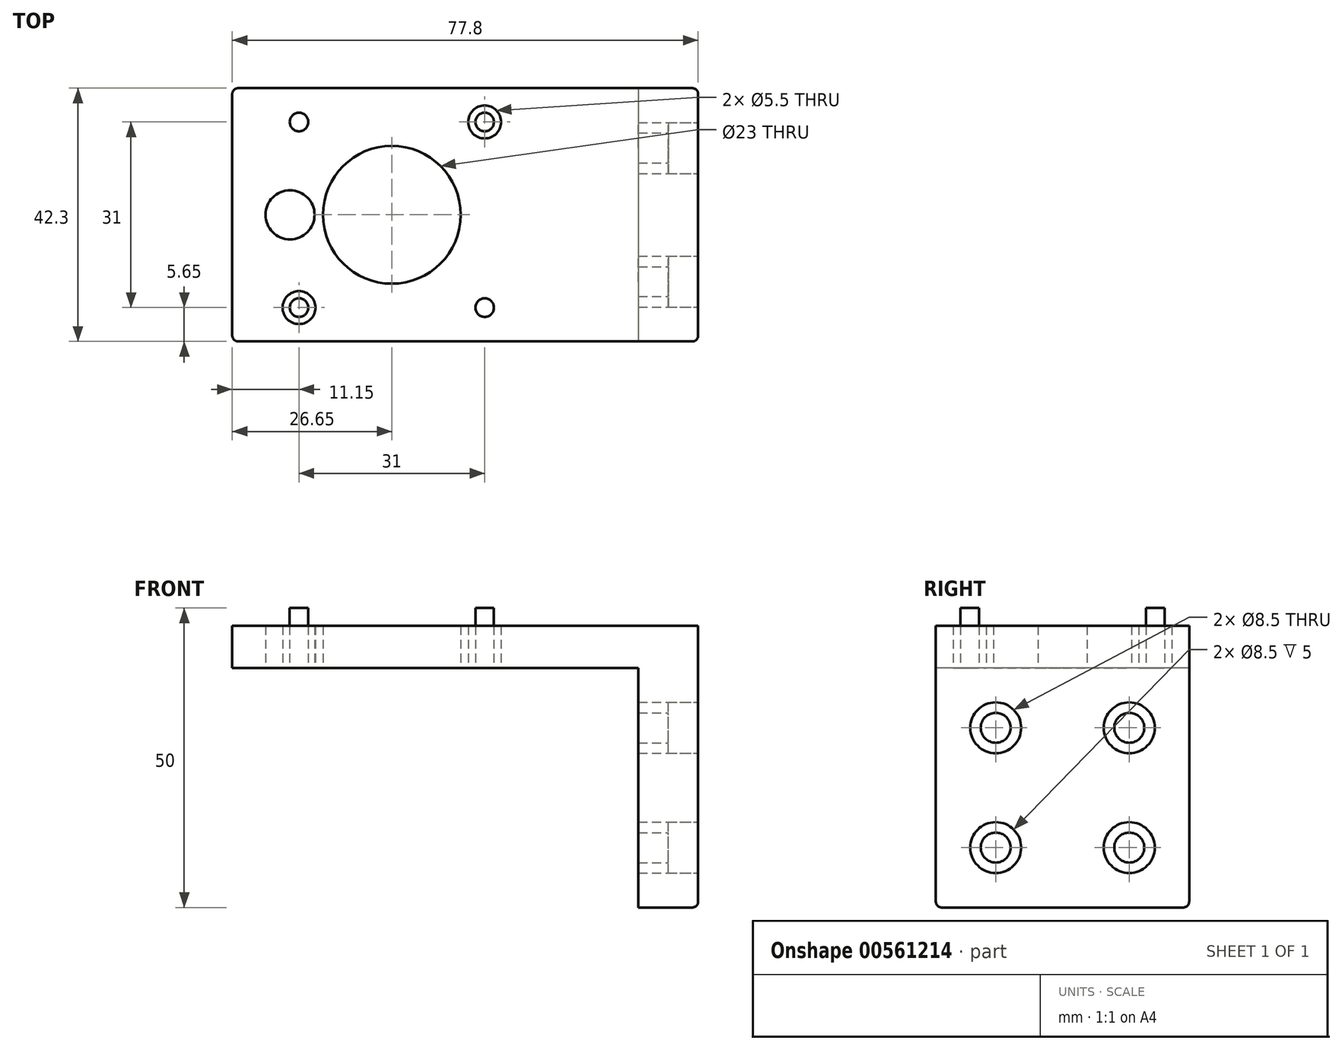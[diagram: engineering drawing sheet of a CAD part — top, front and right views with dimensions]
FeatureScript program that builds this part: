
annotation { "Feature Type Name" : "Feature", "Feature Type Description" : "" }
export const myFeature = defineFeature(function(context is Context, id is Id, definition is map)
    precondition{}
    {
        {
            var Q0;
            Q0=qCreatedBy(makeId("Top.planeOp"),FACE);
            var sketch = newSketch(context, id + "F0", { "sketchPlane" : qUnion([Q0])});
            skCircle(sketch, "E0", {"center": v(0, 0) * mm, "radius": 11.5 * mm});
            skLineSegment(sketch, "E1.bottom", {"start": v(21.15, 21.15) * mm, "end": v(-21.15, 21.15) * mm});
            skLineSegment(sketch, "E1.top", {"start": v(21.15, -21.15) * mm, "end": v(-21.15, -21.15) * mm});
            skLineSegment(sketch, "E1.left", {"start": v(21.15, 21.15) * mm, "end": v(21.15, -21.15) * mm});
            skLineSegment(sketch, "E1.right", {"start": v(-21.15, 21.15) * mm, "end": v(-21.15, -21.15) * mm});
            skCircle(sketch, "E2", {"center": v(-15.5, 15.5) * mm, "radius": 1.55 * mm});
            skLineSegment(sketch, "E3", {"start": v(0, 21.15) * mm, "end": v(0, -21.15) * mm, "construction": true});
            skLineSegment(sketch, "E4", {"start": v(-21.15, 0) * mm, "end": v(21.15, 0) * mm, "construction": true});
            skCircle(sketch, "E5.MirrorC", {"center": v(-15.5, -15.5) * mm, "radius": 1.55 * mm});
            skCircle(sketch, "E6.MirrorC", {"center": v(15.5, 15.5) * mm, "radius": 1.55 * mm});
            skCircle(sketch, "E7.MirrorC", {"center": v(15.5, -15.5) * mm, "radius": 1.55 * mm});
            skLineSegment(sketch, "E8", {"start": v(21.15, 21.15) * mm, "end": v(41.15, 21.15) * mm});
            skLineSegment(sketch, "E9", {"start": v(41.15, 21.15) * mm, "end": v(41.15, -21.15) * mm});
            skLineSegment(sketch, "E10", {"start": v(41.15, -21.15) * mm, "end": v(21.15, -21.15) * mm});
            skLineSegment(sketch, "E11", {"start": v(41.15, 21.15) * mm, "end": v(51.15, 21.15) * mm});
            skLineSegment(sketch, "E12", {"start": v(51.15, 21.15) * mm, "end": v(51.15, -21.15) * mm});
            skLineSegment(sketch, "E13", {"start": v(41.15, -21.15) * mm, "end": v(51.15, -21.15) * mm});
            skCircle(sketch, "E14", {"center": v(-17, 0) * mm, "radius": 4.1 * mm});
            skLineSegment(sketch, "E15", {"start": v(-21.15, 21.15) * mm, "end": v(-26.65, 21.15) * mm});
            skLineSegment(sketch, "E16", {"start": v(-26.65, 21.15) * mm, "end": v(-26.65, -21.15) * mm});
            skLineSegment(sketch, "E17", {"start": v(-26.65, -21.15) * mm, "end": v(-21.15, -21.15) * mm});
            skCircle(sketch, "E18", {"center": v(-15.5, 15.5) * mm, "radius": 2.75 * mm});
            skCircle(sketch, "E19.MirrorC", {"center": v(-15.5, -15.5) * mm, "radius": 2.75 * mm});
            skCircle(sketch, "E20.MirrorC", {"center": v(15.5, 15.5) * mm, "radius": 2.75 * mm});
            skCircle(sketch, "E21.MirrorC", {"center": v(15.5, -15.5) * mm, "radius": 2.75 * mm});
            skSolve(sketch);
        }
        {
            var Q0;
            Q0 = qSketchRegion(id + "F0", true);
            var Q1;
            Q1=makeQuery(id+"F0.imprint","IMPRINT",FACE,{"disambiguationData":[TD([[makeQuery(id+"F0.imprint","IMPRINT",EDGE,{"derivedFrom":sQuery(id+"F0.wireOp",EDGE,"E2")}),-1.0]])]});
            var Q2;
            Q2=makeQuery(id+"F0.imprint","IMPRINT",FACE,{"disambiguationData":[TD([[makeQuery(id+"F0.imprint","IMPRINT",EDGE,{"derivedFrom":sQuery(id+"F0.wireOp",EDGE,"E7.MirrorC")}),-1.0]])]});
            var Q3;
            Q3=makeQuery(id+"F0.imprint","IMPRINT",FACE,{"disambiguationData":[TD([[makeQuery(id+"F0.imprint","IMPRINT",EDGE,{"derivedFrom":sQuery(id+"F0.wireOp",EDGE,"E5.MirrorC")}),1.0]])]});
            var Q4;
            Q4=makeQuery(id+"F0.imprint","IMPRINT",FACE,{"disambiguationData":[TD([[makeQuery(id+"F0.imprint","IMPRINT",EDGE,{"derivedFrom":sQuery(id+"F0.wireOp",EDGE,"E6.MirrorC")}),1.0]])]});
            extrude(context, id + "F1", {"entities" : qUnion([Q0, Q1, Q2, Q3, Q4]), "depth" : 10 * mm, "offsetDistance" : 25 * mm});
        }
        {
            var Q0;
            Q0=makeQuery(id+"F0.imprint","IMPRINT",FACE,{"disambiguationData":[TD([[makeQuery(id+"F0.imprint","IMPRINT",EDGE,{"derivedFrom":sQuery(id+"F0.wireOp",EDGE,"E9")}),1.0]])]});
            extrude(context, id + "F2", {"entities" : qUnion([Q0]), "operationType" : NewBodyOperationType.ADD, "oppositeDirection" : true, "depth" : 40 * mm, "offsetDistance" : 25 * mm});
        }
        {
            var Q0;
            {var subQ0=sQuery(id+"F0.wireOp",EDGE,"E12");Q0=makeQuery(id+"F2.boolean.opBoolean","MERGE",FACE,{"derivedFrom":[makeQuery(id+"F1.opExtrude","SWEPT_FACE",FACE,{"disambiguationData":[OSD([subQ0])]}),makeQuery(id+"F2.opExtrude","SWEPT_FACE",FACE,{"disambiguationData":[OSD([subQ0])]})]});}
            var sketch = newSketch(context, id + "F3", { "sketchPlane" : qUnion([Q0])});
            skCircle(sketch, "E22", {"center": v(-11.15, -30) * mm, "radius": 4.25 * mm});
            skCircle(sketch, "E23", {"center": v(-11.15, -30) * mm, "radius": 2.5 * mm});
            skLineSegment(sketch, "E24", {"start": v(0, 10) * mm, "end": v(0, -40) * mm, "construction": true});
            skCircle(sketch, "E25.MirrorC", {"center": v(11.15, -30) * mm, "radius": 2.5 * mm});
            skCircle(sketch, "E26.MirrorC", {"center": v(11.15, -30) * mm, "radius": 4.25 * mm});
            skLineSegment(sketch, "E27", {"start": v(11.15, -30) * mm, "end": v(11.15, -20) * mm, "construction": true});
            skLineSegment(sketch, "E28", {"start": v(-11.15, -30) * mm, "end": v(-11.15, -20) * mm, "construction": true});
            skLineSegment(sketch, "E29", {"start": v(-11.15, -20) * mm, "end": v(11.15, -20) * mm, "construction": true});
            skCircle(sketch, "E30.MirrorC", {"center": v(-11.15, -10) * mm, "radius": 2.5 * mm});
            skCircle(sketch, "E31.MirrorC", {"center": v(-11.15, -10) * mm, "radius": 4.25 * mm});
            skCircle(sketch, "E32.MirrorC", {"center": v(11.15, -10) * mm, "radius": 4.25 * mm});
            skCircle(sketch, "E33.MirrorC", {"center": v(11.15, -10) * mm, "radius": 2.5 * mm});
            skSolve(sketch);
        }
        {
            var Q0;
            Q0=makeQuery(id+"F3.imprint","IMPRINT",FACE,{"disambiguationData":[TD([[makeQuery(id+"F3.imprint","IMPRINT",EDGE,{"derivedFrom":sQuery(id+"F3.wireOp",EDGE,"E30.MirrorC")}),-1.0]])]});
            var Q1;
            Q1=makeQuery(id+"F3.imprint","IMPRINT",FACE,{"disambiguationData":[TD([[makeQuery(id+"F3.imprint","IMPRINT",EDGE,{"derivedFrom":sQuery(id+"F3.wireOp",EDGE,"E33.MirrorC")}),1.0]])]});
            var Q2;
            Q2=makeQuery(id+"F3.imprint","IMPRINT",FACE,{"disambiguationData":[TD([[makeQuery(id+"F3.imprint","IMPRINT",EDGE,{"derivedFrom":sQuery(id+"F3.wireOp",EDGE,"E25.MirrorC")}),-1.0]])]});
            var Q3;
            Q3=makeQuery(id+"F3.imprint","IMPRINT",FACE,{"disambiguationData":[TD([[makeQuery(id+"F3.imprint","IMPRINT",EDGE,{"derivedFrom":sQuery(id+"F3.wireOp",EDGE,"E23")}),1.0]])]});
            extrude(context, id + "F4", {"entities" : qUnion([Q0, Q1, Q2, Q3]), "operationType" : NewBodyOperationType.REMOVE, "endBound" : BoundingType.THROUGH_ALL, "oppositeDirection" : true, "depth" : 25 * mm, "offsetDistance" : 25 * mm});
        }
        {
            var Q0;
            Q0=makeQuery(id+"F3.imprint","IMPRINT",FACE,{"disambiguationData":[TD([[makeQuery(id+"F3.imprint","IMPRINT",EDGE,{"derivedFrom":sQuery(id+"F3.wireOp",EDGE,"E30.MirrorC")}),1.0]])]});
            var Q1;
            Q1=makeQuery(id+"F3.imprint","IMPRINT",FACE,{"disambiguationData":[TD([[makeQuery(id+"F3.imprint","IMPRINT",EDGE,{"derivedFrom":sQuery(id+"F3.wireOp",EDGE,"E32.MirrorC")}),1.0]])]});
            var Q2;
            Q2=makeQuery(id+"F3.imprint","IMPRINT",FACE,{"disambiguationData":[TD([[makeQuery(id+"F3.imprint","IMPRINT",EDGE,{"derivedFrom":sQuery(id+"F3.wireOp",EDGE,"E25.MirrorC")}),1.0]])]});
            var Q3;
            Q3=makeQuery(id+"F3.imprint","IMPRINT",FACE,{"disambiguationData":[TD([[makeQuery(id+"F3.imprint","IMPRINT",EDGE,{"derivedFrom":sQuery(id+"F3.wireOp",EDGE,"E22")}),1.0]])]});
            extrude(context, id + "F5", {"entities" : qUnion([Q0, Q1, Q2, Q3]), "operationType" : NewBodyOperationType.REMOVE, "oppositeDirection" : true, "depth" : 5 * mm, "offsetDistance" : 25 * mm});
        }
        {
            var Q0;
            Q0=makeQuery(id+"F1.opExtrude","CAP_FACE",FACE,{"disambiguationData":[OSD([sQuery(id+"F0.wireOp",EDGE,"E0"),sQuery(id+"F0.wireOp",EDGE,"E1.bottom"),sQuery(id+"F0.wireOp",EDGE,"E1.top"),sQuery(id+"F0.wireOp",EDGE,"E2"),sQuery(id+"F0.wireOp",EDGE,"E5.MirrorC"),sQuery(id+"F0.wireOp",EDGE,"E6.MirrorC"),sQuery(id+"F0.wireOp",EDGE,"E7.MirrorC"),sQuery(id+"F0.wireOp",EDGE,"E8"),sQuery(id+"F0.wireOp",EDGE,"E10"),sQuery(id+"F0.wireOp",EDGE,"E11"),sQuery(id+"F0.wireOp",EDGE,"E12"),sQuery(id+"F0.wireOp",EDGE,"E13"),sQuery(id+"F0.wireOp",EDGE,"E14"),sQuery(id+"F0.wireOp",EDGE,"E15"),sQuery(id+"F0.wireOp",EDGE,"E16"),sQuery(id+"F0.wireOp",EDGE,"E17")])],"isStart":false});
            var sketch = newSketch(context, id + "F6", { "sketchPlane" : qUnion([Q0])});
            skCircle(sketch, "E34.0", {"center": v(15.5, 15.5) * mm, "radius": 2.75 * mm});
            skCircle(sketch, "E34.1", {"center": v(-15.5, 15.5) * mm, "radius": 2.75 * mm});
            skCircle(sketch, "E34.2", {"center": v(-15.5, -15.5) * mm, "radius": 2.75 * mm});
            skCircle(sketch, "E34.3", {"center": v(15.5, -15.5) * mm, "radius": 2.75 * mm});
            skSolve(sketch);
        }
        {
            var Q0;
            {var subQ0=sQuery(id+"F0.wireOp",EDGE,"E13");var subQ1=sQuery(id+"F0.wireOp",EDGE,"E12");Q0=makeQuery(id+"F2.boolean.opBoolean","MERGE",EDGE,{"derivedFrom":[makeQuery(id+"F1.opExtrude","SWEPT_EDGE",EDGE,{"disambiguationData":[OSD([subQ1,subQ0])]}),makeQuery(id+"F2.opExtrude","SWEPT_EDGE",EDGE,{"disambiguationData":[OSD([subQ1,subQ0])]})]});}
            var Q1;
            {var subQ0=sQuery(id+"F0.wireOp",EDGE,"E12");var subQ1=sQuery(id+"F0.wireOp",EDGE,"E11");Q1=makeQuery(id+"F2.boolean.opBoolean","MERGE",EDGE,{"derivedFrom":[makeQuery(id+"F1.opExtrude","SWEPT_EDGE",EDGE,{"disambiguationData":[OSD([subQ1,subQ0])]}),makeQuery(id+"F2.opExtrude","SWEPT_EDGE",EDGE,{"disambiguationData":[OSD([subQ1,subQ0])]})]});}
            var Q2;
            Q2=makeQuery(id+"F2.opExtrude","CAP_EDGE",EDGE,{"disambiguationData":[OSD([sQuery(id+"F0.wireOp",EDGE,"E12")])],"isStart":false});
            var Q3;
            Q3=makeQuery(id+"F1.opExtrude","CAP_EDGE",EDGE,{"disambiguationData":[OSD([sQuery(id+"F0.wireOp",EDGE,"E12")])],"isStart":false});
            var Q4;
            Q4=makeQuery(id+"F1.opExtrude","CAP_EDGE",EDGE,{"disambiguationData":[OSD([sQuery(id+"F0.wireOp",EDGE,"E1.bottom"),sQuery(id+"F0.wireOp",EDGE,"E8"),sQuery(id+"F0.wireOp",EDGE,"E11"),sQuery(id+"F0.wireOp",EDGE,"E15")])],"isStart":false});
            var Q5;
            Q5=makeQuery(id+"F1.opExtrude","CAP_EDGE",EDGE,{"disambiguationData":[OSD([sQuery(id+"F0.wireOp",EDGE,"E1.top"),sQuery(id+"F0.wireOp",EDGE,"E10"),sQuery(id+"F0.wireOp",EDGE,"E13"),sQuery(id+"F0.wireOp",EDGE,"E17")])],"isStart":false});
            var Q6;
            Q6=makeQuery(id+"F1.opExtrude","CAP_EDGE",EDGE,{"disambiguationData":[OSD([sQuery(id+"F0.wireOp",EDGE,"E16")])],"isStart":false});
            var Q7;
            Q7=makeQuery(id+"F1.opExtrude","SWEPT_EDGE",EDGE,{"disambiguationData":[OSD([sQuery(id+"F0.wireOp",EDGE,"E15"),sQuery(id+"F0.wireOp",EDGE,"E16")])]});
            var Q8;
            Q8=makeQuery(id+"F1.opExtrude","SWEPT_EDGE",EDGE,{"disambiguationData":[OSD([sQuery(id+"F0.wireOp",EDGE,"E16"),sQuery(id+"F0.wireOp",EDGE,"E17")])]});
            var Q9;
            Q9=makeQuery(id+"F2.opExtrude","CAP_EDGE",EDGE,{"disambiguationData":[OSD([sQuery(id+"F0.wireOp",EDGE,"E11")])],"isStart":false});
            var Q10;
            Q10=makeQuery(id+"F2.opExtrude","CAP_EDGE",EDGE,{"disambiguationData":[OSD([sQuery(id+"F0.wireOp",EDGE,"E13")])],"isStart":false});
            fillet(context, id + "F7", {"entities" : qUnion([Q0, Q1, Q2, Q3, Q4, Q5, Q6, Q7, Q8, Q9, Q10]), "radius" : 1 * mm, "tangentPropagation" : true, "allowEdgeOverflow" : false});
        }
        {
            var Q0;
            Q0=makeQuery(id+"F1.opExtrude","CAP_EDGE",EDGE,{"disambiguationData":[OSD([sQuery(id+"F0.wireOp",EDGE,"E14")])],"isStart":false});
            var Q1;
            Q1=makeQuery(id+"F1.opExtrude","CAP_EDGE",EDGE,{"disambiguationData":[OSD([sQuery(id+"F0.wireOp",EDGE,"E0")])],"isStart":false});
            fillet(context, id + "F8", {"entities" : qUnion([Q0, Q1]), "radius" : 0.5 * mm, "tangentPropagation" : true, "allowEdgeOverflow" : false});
        }
        {
            var Q0;
            Q0=makeQuery(id+"F6.imprint","IMPRINT",FACE,{"disambiguationData":[TD([[makeQuery(id+"F6.imprint","IMPRINT",EDGE,{"derivedFrom":sQuery(id+"F6.wireOp",EDGE,"E34.0")}),-1.0]])]});
            var Q1;
            Q1=makeQuery(id+"F6.imprint","IMPRINT",FACE,{"disambiguationData":[TD([[makeQuery(id+"F6.imprint","IMPRINT",EDGE,{"derivedFrom":sQuery(id+"F6.wireOp",EDGE,"E34.3")}),1.0]])]});
            var Q2;
            Q2=makeQuery(id+"F6.imprint","IMPRINT",FACE,{"disambiguationData":[TD([[makeQuery(id+"F6.imprint","IMPRINT",EDGE,{"derivedFrom":sQuery(id+"F6.wireOp",EDGE,"E34.2")}),-1.0]])]});
            var Q3;
            Q3=makeQuery(id+"F6.imprint","IMPRINT",FACE,{"disambiguationData":[TD([[makeQuery(id+"F6.imprint","IMPRINT",EDGE,{"derivedFrom":sQuery(id+"F6.wireOp",EDGE,"E34.1")}),1.0]])]});
            extrude(context, id + "F9", {"entities" : qUnion([Q0, Q1, Q2, Q3]), "operationType" : NewBodyOperationType.REMOVE, "oppositeDirection" : true, "depth" : 3 * mm, "offsetDistance" : 25 * mm});
        }
    });
